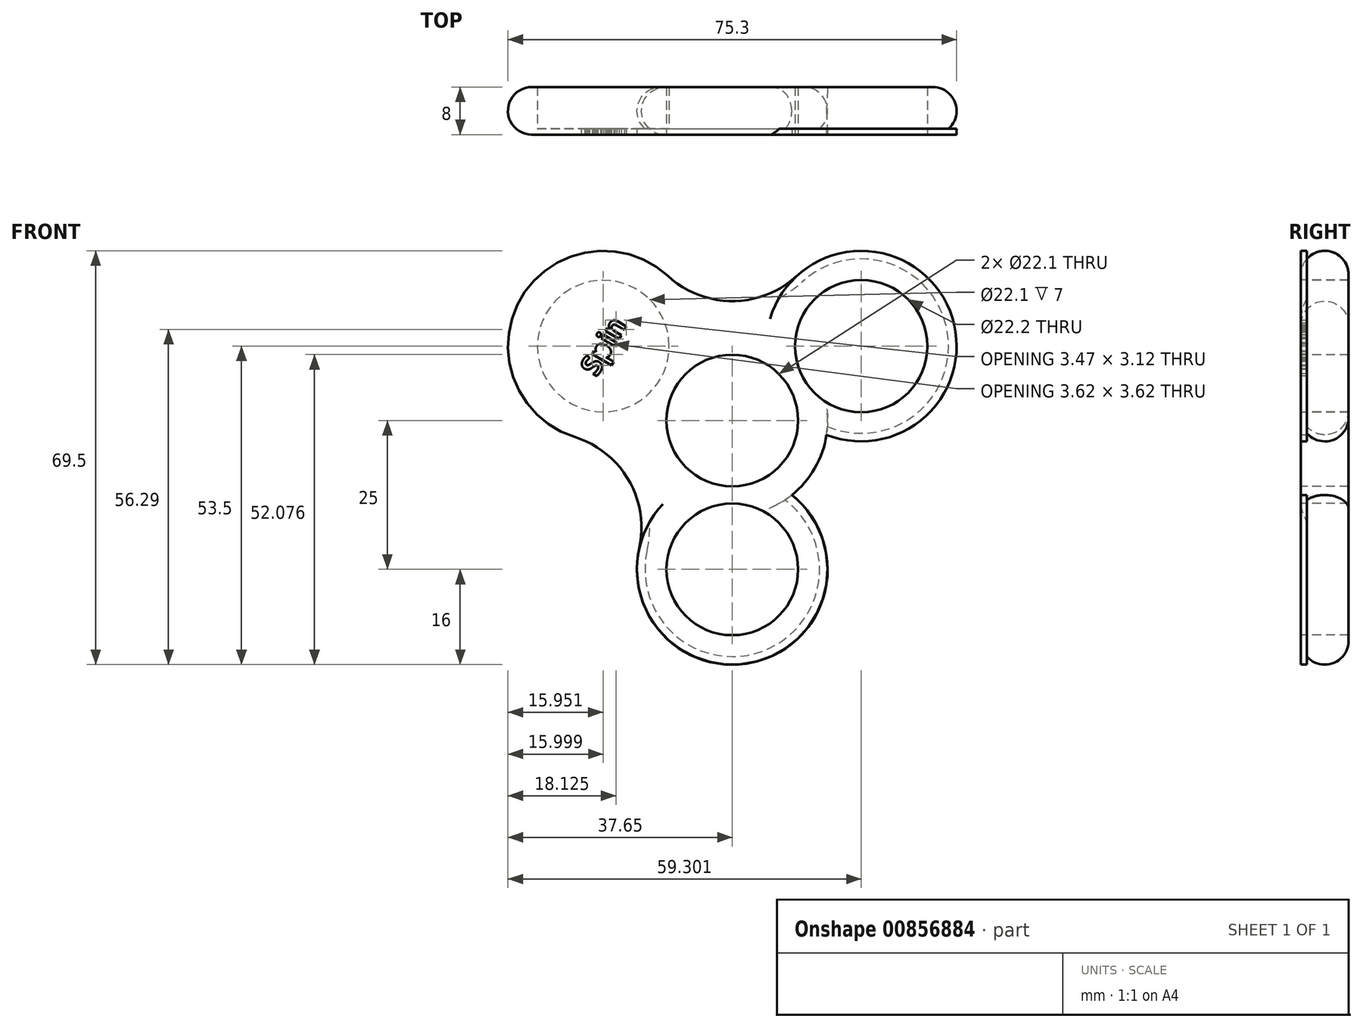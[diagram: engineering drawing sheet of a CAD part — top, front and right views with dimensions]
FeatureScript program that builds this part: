
annotation { "Feature Type Name" : "Feature", "Feature Type Description" : "" }
export const myFeature = defineFeature(function(context is Context, id is Id, definition is map)
    precondition{}
    {
        {
            var Q0;
            Q0=qCreatedBy(makeId("Front.planeOp"),FACE);
            var sketch = newSketch(context, id + "F0", { "sketchPlane" : qUnion([Q0])});
            skCircle(sketch, "E0", {"center": v(0, 0) * mm, "radius": 16 * mm});
            skCircle(sketch, "E1", {"center": v(0, 0) * mm, "radius": 11.05 * mm});
            skCircle(sketch, "E2", {"center": v(-21.65, 12.5) * mm, "radius": 16 * mm});
            skCircle(sketch, "E3", {"center": v(-21.65, 12.5) * mm, "radius": 11.05 * mm});
            skCircle(sketch, "E4", {"center": v(21.65, 12.5) * mm, "radius": 16 * mm});
            skCircle(sketch, "E5", {"center": v(21.65, 12.5) * mm, "radius": 11.1 * mm});
            skCircle(sketch, "E6", {"center": v(0, -25) * mm, "radius": 16 * mm});
            skCircle(sketch, "E7", {"center": v(0, -25) * mm, "radius": 11.05 * mm});
            skLineSegment(sketch, "E8", {"start": v(-21.65, 12.5) * mm, "end": v(0, 0) * mm, "construction": true});
            skLineSegment(sketch, "E9", {"start": v(21.65, 12.5) * mm, "end": v(0, 0) * mm, "construction": true});
            skLineSegment(sketch, "E10", {"start": v(0, -25) * mm, "end": v(0, 0) * mm, "construction": true});
            skLineSegment(sketch, "E11", {"start": v(0, 0) * mm, "end": v(-46.7, -26.96) * mm, "construction": true});
            skLineSegment(sketch, "E12", {"start": v(0, 44.23) * mm, "end": v(0, 0) * mm, "construction": true});
            skLineSegment(sketch, "E13.MirrorCS", {"start": v(0, 0) * mm, "end": v(46.7, -26.96) * mm, "construction": true});
            skArc(sketch, "E14", {"start": v(-15.62, -21.52) * mm, "mid": v(-17.38, -10.03) * mm, "end": v(-26.44, -2.77) * mm});
            skArc(sketch, "E15.MirrorCS", {"start": v(15.62, -21.52) * mm, "mid": v(17.38, -10.03) * mm, "end": v(26.44, -2.77) * mm});
            skArc(sketch, "E16.MirrorCS", {"start": v(-10.83, 24.28) * mm, "mid": v(0, 20.06) * mm, "end": v(10.83, 24.28) * mm});
            skText(sketch, "E17", { "text": "Egor", "fontName": "OpenSans-Bold.ttf"});
            skText(sketch, "E18", { "text": "Spin", "fontName": "OpenSans-Bold.ttf"});
            skText(sketch, "E19", { "text": "V2", "fontName": "OpenSans-Bold.ttf"});
            const initialGuessF0  = {"E17": [0.00537, -0.02314, -1, 0, 0.00345], "E18": [-0.02275, 0.00723, 0.5, 0.86603, 0.00345], "E19": [0.01907, 0.0142, 0.5, -0.86603, 0.00345]};
            skSetInitialGuess(sketch, initialGuessF0);
            skSolve(sketch);
        }
        {
            var Q0;
            Q0=makeQuery(id+"F0.imprint","IMPRINT",FACE,{"disambiguationData":[TD([[makeQuery(id+"F0.imprint","IMPRINT",EDGE,{"derivedFrom":sQuery(id+"F0.wireOp",EDGE,"E1")}),-1.0]])]});
            var Q1;
            {var subQ0=sQuery(id+"F0.wireOp",EDGE,"E2");var subQ1=sQuery(id+"F0.wireOp",EDGE,"E0");var subQ2=makeQuery(id+"F0.imprint","INTERSECT",VERTEX,{"disambiguationData":[OD(0.0)],"derivedFrom":[subQ1,subQ0]});Q1=makeQuery(id+"F0.imprint","IMPRINT",FACE,{"disambiguationData":[TD([[makeQuery(id+"F0.imprint","IMPRINT",EDGE,{"disambiguationData":[TD([[subQ2,-1.0]])],"derivedFrom":subQ1}),1.0]])]});}
            var Q2;
            {var subQ5=sQuery(id+"F0.wireOp",EDGE,"E16.MirrorCS");Q2=makeQuery(id+"F0.imprint","IMPRINT",FACE,{"disambiguationData":[TD([[makeQuery(id+"F0.imprint","IMPRINT",EDGE,{"derivedFrom":subQ5}),-1.0]])]});}
            var Q3;
            Q3=makeQuery(id+"F0.imprint","IMPRINT",FACE,{"disambiguationData":[TD([[makeQuery(id+"F0.imprint","IMPRINT",EDGE,{"derivedFrom":sQuery(id+"F0.wireOp",EDGE,"E3")}),-1.0]])]});
            var Q4;
            {var subQ5=sQuery(id+"F0.wireOp",EDGE,"E14");Q4=makeQuery(id+"F0.imprint","IMPRINT",FACE,{"disambiguationData":[TD([[makeQuery(id+"F0.imprint","IMPRINT",EDGE,{"derivedFrom":subQ5}),-1.0]])]});}
            var Q5;
            {var subQ0=sQuery(id+"F0.wireOp",EDGE,"E6");var subQ1=sQuery(id+"F0.wireOp",EDGE,"E0");var subQ2=makeQuery(id+"F0.imprint","INTERSECT",VERTEX,{"disambiguationData":[OD(0.0)],"derivedFrom":[subQ1,subQ0]});Q5=makeQuery(id+"F0.imprint","IMPRINT",FACE,{"disambiguationData":[TD([[makeQuery(id+"F0.imprint","IMPRINT",EDGE,{"disambiguationData":[TD([[subQ2,-1.0]])],"derivedFrom":subQ1}),1.0]])]});}
            var Q6;
            Q6=makeQuery(id+"F0.imprint","IMPRINT",FACE,{"disambiguationData":[TD([[makeQuery(id+"F0.imprint","IMPRINT",EDGE,{"derivedFrom":sQuery(id+"F0.wireOp",EDGE,"E7")}),-1.0]])]});
            var Q7;
            {var subQ5=sQuery(id+"F0.wireOp",EDGE,"E15.MirrorCS");Q7=makeQuery(id+"F0.imprint","IMPRINT",FACE,{"disambiguationData":[TD([[makeQuery(id+"F0.imprint","IMPRINT",EDGE,{"derivedFrom":subQ5}),1.0]])]});}
            var Q8;
            {var subQ0=sQuery(id+"F0.wireOp",EDGE,"E4");var subQ1=sQuery(id+"F0.wireOp",EDGE,"E0");var subQ2=makeQuery(id+"F0.imprint","INTERSECT",VERTEX,{"disambiguationData":[OD(0.0)],"derivedFrom":[subQ1,subQ0]});Q8=makeQuery(id+"F0.imprint","IMPRINT",FACE,{"disambiguationData":[TD([[makeQuery(id+"F0.imprint","IMPRINT",EDGE,{"disambiguationData":[TD([[subQ2,1.0]])],"derivedFrom":subQ1}),1.0]])]});}
            var Q9;
            Q9=makeQuery(id+"F0.imprint","IMPRINT",FACE,{"disambiguationData":[TD([[makeQuery(id+"F0.imprint","IMPRINT",EDGE,{"derivedFrom":sQuery(id+"F0.wireOp",EDGE,"E5")}),-1.0]])]});
            extrude(context, id + "F1", {"entities" : qUnion([Q0, Q1, Q2, Q3, Q4, Q5, Q6, Q7, Q8, Q9]), "oppositeDirection" : true, "depth" : 8 * mm, "offsetDistance" : 25 * mm});
        }
        {
            var Q0;
            Q0=makeQuery(id+"F1.opExtrude","CAP_EDGE",EDGE,{"disambiguationData":[OSD([sQuery(id+"F0.wireOp",EDGE,"E16.MirrorCS")])],"isStart":false});
            var Q1;
            Q1=makeQuery(id+"F1.opExtrude","CAP_EDGE",EDGE,{"disambiguationData":[OSD([sQuery(id+"F0.wireOp",EDGE,"E4")])],"isStart":true});
            fillet(context, id + "F2", {"entities" : qUnion([Q0, Q1]), "radius" : 4 * mm, "tangentPropagation" : true, "allowEdgeOverflow" : false});
        }
        {
            var Q0;
            {var subQ0=sQuery(id+"F0.wireOp",EDGE,"E5");var subQ1=sQuery(id+"F0.wireOp",EDGE,"E0");var subQ2=makeQuery(id+"F0.imprint","INTERSECT",VERTEX,{"disambiguationData":[OD(0.0)],"derivedFrom":[subQ1,subQ0]});Q0=makeQuery(id+"F0.imprint","IMPRINT",FACE,{"disambiguationData":[TD([[makeQuery(id+"F0.imprint","IMPRINT",EDGE,{"disambiguationData":[TD([[subQ2,1.0]])],"derivedFrom":subQ1}),-1.0]])]});}
            var Q1;
            {var subQ0=sQuery(id+"F0.wireOp",EDGE,"E5");var subQ1=sQuery(id+"F0.wireOp",EDGE,"E0");var subQ2=makeQuery(id+"F0.imprint","INTERSECT",VERTEX,{"disambiguationData":[OD(0.0)],"derivedFrom":[subQ1,subQ0]});Q1=makeQuery(id+"F0.imprint","IMPRINT",FACE,{"disambiguationData":[TD([[makeQuery(id+"F0.imprint","IMPRINT",EDGE,{"disambiguationData":[TD([[subQ2,1.0]])],"derivedFrom":subQ1}),1.0]])]});}
            var Q2;
            {var subQ0=sQuery(id+"F0.wireOp",EDGE,"E3");var subQ1=sQuery(id+"F0.wireOp",EDGE,"E0");var subQ2=makeQuery(id+"F0.imprint","INTERSECT",VERTEX,{"disambiguationData":[OD(0.0)],"derivedFrom":[subQ1,subQ0]});Q2=makeQuery(id+"F0.imprint","IMPRINT",FACE,{"disambiguationData":[TD([[makeQuery(id+"F0.imprint","IMPRINT",EDGE,{"disambiguationData":[TD([[subQ2,-1.0]])],"derivedFrom":subQ1}),-1.0]])]});}
            var Q3;
            {var subQ0=sQuery(id+"F0.wireOp",EDGE,"E3");var subQ1=sQuery(id+"F0.wireOp",EDGE,"E0");var subQ2=makeQuery(id+"F0.imprint","INTERSECT",VERTEX,{"disambiguationData":[OD(0.0)],"derivedFrom":[subQ1,subQ0]});Q3=makeQuery(id+"F0.imprint","IMPRINT",FACE,{"disambiguationData":[TD([[makeQuery(id+"F0.imprint","IMPRINT",EDGE,{"disambiguationData":[TD([[subQ2,-1.0]])],"derivedFrom":subQ1}),1.0]])]});}
            var Q4;
            {var subQ0=sQuery(id+"F0.wireOp",EDGE,"E7");var subQ1=sQuery(id+"F0.wireOp",EDGE,"E0");var subQ2=makeQuery(id+"F0.imprint","INTERSECT",VERTEX,{"disambiguationData":[OD(0.0)],"derivedFrom":[subQ1,subQ0]});Q4=makeQuery(id+"F0.imprint","IMPRINT",FACE,{"disambiguationData":[TD([[makeQuery(id+"F0.imprint","IMPRINT",EDGE,{"disambiguationData":[TD([[subQ2,-1.0]])],"derivedFrom":subQ1}),-1.0]])]});}
            var Q5;
            {var subQ0=sQuery(id+"F0.wireOp",EDGE,"E7");var subQ1=sQuery(id+"F0.wireOp",EDGE,"E0");var subQ2=makeQuery(id+"F0.imprint","INTERSECT",VERTEX,{"disambiguationData":[OD(0.0)],"derivedFrom":[subQ1,subQ0]});Q5=makeQuery(id+"F0.imprint","IMPRINT",FACE,{"disambiguationData":[TD([[makeQuery(id+"F0.imprint","IMPRINT",EDGE,{"disambiguationData":[TD([[subQ2,-1.0]])],"derivedFrom":subQ1}),1.0]])]});}
            extrude(context, id + "F3", {"entities" : qUnion([Q0, Q1, Q2, Q3, Q4, Q5]), "operationType" : NewBodyOperationType.ADD, "oppositeDirection" : true, "depth" : 1 * mm, "offsetDistance" : 25 * mm});
        }
    });
